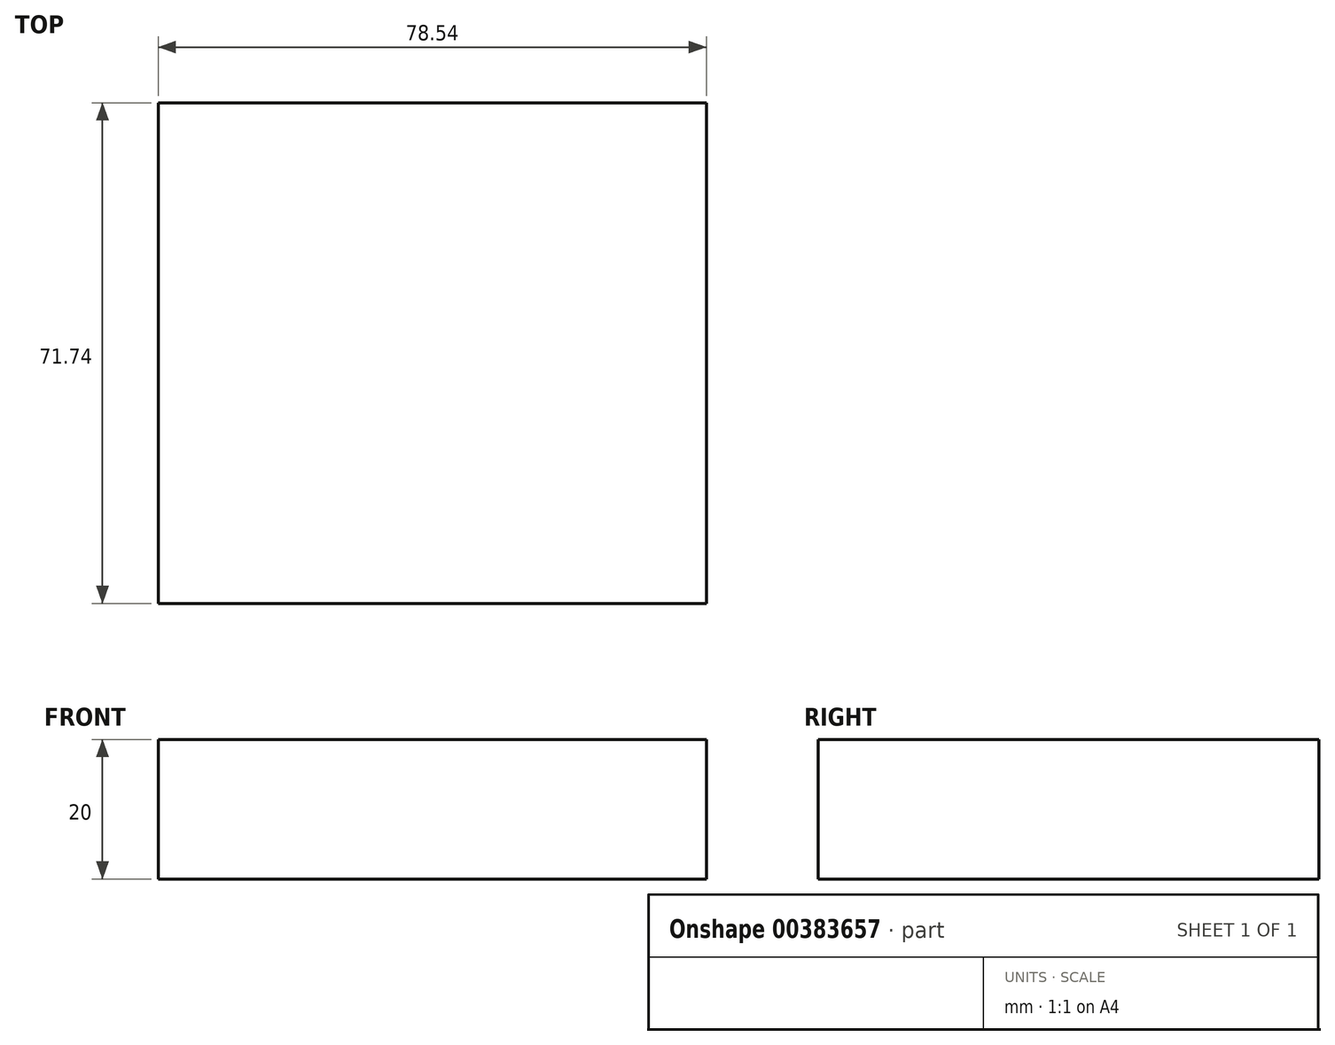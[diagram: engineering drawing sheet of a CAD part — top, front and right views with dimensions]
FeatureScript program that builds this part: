
annotation { "Feature Type Name" : "Feature", "Feature Type Description" : "" }
export const myFeature = defineFeature(function(context is Context, id is Id, definition is map)
    precondition{}
    {
        {
            var Q0;
            Q0=qCreatedBy(makeId("Top.planeOp"),FACE);
            var sketch = newSketch(context, id + "F0", { "sketchPlane" : qUnion([Q0])});
            skLineSegment(sketch, "E0.bottom", {"start": v(-39.27, 35.87) * mm, "end": v(39.27, 35.87) * mm});
            skLineSegment(sketch, "E0.top", {"start": v(-39.27, -35.87) * mm, "end": v(39.27, -35.87) * mm});
            skLineSegment(sketch, "E0.left", {"start": v(-39.27, 35.87) * mm, "end": v(-39.27, -35.87) * mm});
            skLineSegment(sketch, "E0.right", {"start": v(39.27, 35.87) * mm, "end": v(39.27, -35.87) * mm});
            skPoint(sketch, "E1", {"position": v(0, 35.87) * mm});
            skPoint(sketch, "E2", {"position": v(39.27, 0) * mm});
            skSolve(sketch);
        }
        {
            var Q0;
            Q0=makeQuery(id+"F0.imprint","IMPRINT",FACE,{"disambiguationData":[TD([[makeQuery(id+"F0.imprint","IMPRINT",EDGE,{"derivedFrom":sQuery(id+"F0.wireOp",EDGE,"E0.bottom")}),-1.0]])]});
            extrude(context, id + "F1", {"entities" : qUnion([Q0]), "depth" : 20 * mm});
        }
    });
